FCSTD DOCUMENT  (FreeCAD 1.0R39109 (Git))
Label: L_Boxx_Old_Lid_Template
License: All rights reserved
LicenseURL: https://en.wikipedia.org/wiki/All_rights_reserved
objects: Sketcher::SketchObject×2, PartDesign::Body×1
note: 5 computed .brp shape members not serialized (recipe doc carries the construction recipe); baked Part::Feature solids carry a one-line shape summary decoded from their .brp

FEATURE [Sketcher::SketchObject] Sketch  label="SketchCutout"
  ArcFitTolerance = 0
  AttachmentSupport = -> [XY_Plane]
  FullyConstrained = true
  MakeInternals = false
  MapMode = 5
  expr: Constraints[62] = .Constraints.height
  expr: Constraints[63] = .Constraints.width / 2
  sketch-geometry (80):
    g0: LineSegment StartX=0 StartY=0 StartZ=0 EndX=0 EndY=30 EndZ=0
    g1: LineSegment StartX=0 StartY=30 StartZ=0 EndX=7 EndY=30 EndZ=0
    g2: LineSegment StartX=7 StartY=30 StartZ=0 EndX=7 EndY=49 EndZ=0
    g3: LineSegment StartX=7 StartY=49 StartZ=0 EndX=0 EndY=49 EndZ=0
    g4: LineSegment StartX=0 StartY=49 StartZ=0 EndX=0 EndY=123 EndZ=0
    g5: LineSegment StartX=0 StartY=123 StartZ=0 EndX=5 EndY=127 EndZ=0
    g6: LineSegment StartX=5 StartY=127 StartZ=0 EndX=5 EndY=147.5 EndZ=0
    g7: LineSegment StartX=5 StartY=147.5 StartZ=0 EndX=11 EndY=147.5 EndZ=0
    g8: LineSegment StartX=11 StartY=147.5 StartZ=0 EndX=11 EndY=166.5 EndZ=0
    g9: LineSegment StartX=11 StartY=166.5 StartZ=0 EndX=5 EndY=166.5 EndZ=0
    g10: LineSegment StartX=5 StartY=166.5 StartZ=0 EndX=5 EndY=187 EndZ=0
    g11: LineSegment StartX=5 StartY=187 StartZ=0 EndX=0 EndY=191 EndZ=0
    g12: LineSegment StartX=0 StartY=191 StartZ=0 EndX=0 EndY=253 EndZ=0
    g13: LineSegment StartX=0 StartY=253 StartZ=0 EndX=7 EndY=253 EndZ=0
    g14: LineSegment StartX=7 StartY=253 StartZ=0 EndX=7 EndY=272 EndZ=0
    g15: LineSegment StartX=7 StartY=272 StartZ=0 EndX=0 EndY=272 EndZ=0
    g16: LineSegment StartX=0 StartY=272 StartZ=0 EndX=0 EndY=286 EndZ=0
    g17: LineSegment StartX=0 StartY=286 StartZ=0 EndX=20.5 EndY=286 EndZ=0
    g18: LineSegment StartX=20.5 StartY=286 StartZ=0 EndX=20.5 EndY=320 EndZ=0
    g19: LineSegment [constr] StartX=5 StartY=166.5 StartZ=0 EndX=5 EndY=147.5 EndZ=0
    g20: LineSegment StartX=0 StartY=0 StartZ=0 EndX=405 EndY=0 EndZ=0
    g21: LineSegment [constr] StartX=202.5 StartY=0 StartZ=0 EndX=202.5 EndY=320 EndZ=0
    g22: LineSegment StartX=405 StartY=0 StartZ=0 EndX=405 EndY=30 EndZ=0
    g23: LineSegment StartX=405 StartY=30 StartZ=0 EndX=398 EndY=30 EndZ=0
    g24: LineSegment StartX=398 StartY=30 StartZ=0 EndX=398 EndY=49 EndZ=0
    g25: LineSegment StartX=398 StartY=49 StartZ=0 EndX=405 EndY=49 EndZ=0
    g26: LineSegment StartX=405 StartY=49 StartZ=0 EndX=405 EndY=123 EndZ=0
    g27: LineSegment StartX=405 StartY=123 StartZ=0 EndX=400 EndY=127 EndZ=0
    g28: LineSegment StartX=400 StartY=127 StartZ=0 EndX=400 EndY=147.5 EndZ=0
    g29: LineSegment StartX=400 StartY=147.5 StartZ=0 EndX=394 EndY=147.5 EndZ=0
    g30: LineSegment StartX=394 StartY=147.5 StartZ=0 EndX=394 EndY=166.5 EndZ=0
    g31: LineSegment StartX=394 StartY=166.5 StartZ=0 EndX=400 EndY=166.5 EndZ=0
    g32: LineSegment StartX=400 StartY=166.5 StartZ=0 EndX=400 EndY=187 EndZ=0
    g33: LineSegment StartX=400 StartY=187 StartZ=0 EndX=405 EndY=191 EndZ=0
    g34: LineSegment StartX=405 StartY=191 StartZ=0 EndX=405 EndY=253 EndZ=0
    g35: LineSegment StartX=405 StartY=253 StartZ=0 EndX=398 EndY=253 EndZ=0
    g36: LineSegment StartX=398 StartY=253 StartZ=0 EndX=398 EndY=272 EndZ=0
    g37: LineSegment StartX=398 StartY=272 StartZ=0 EndX=405 EndY=272 EndZ=0
    g38: LineSegment StartX=405 StartY=272 StartZ=0 EndX=405 EndY=286 EndZ=0
    g39: LineSegment StartX=405 StartY=286 StartZ=0 EndX=384.5 EndY=286 EndZ=0
    g40: LineSegment StartX=384.5 StartY=286 StartZ=0 EndX=384.5 EndY=320 EndZ=0
    g41: LineSegment [constr] StartX=400 StartY=166.5 StartZ=0 EndX=400 EndY=147.5 EndZ=0
    g42: LineSegment [constr] StartX=20.5 StartY=286 StartZ=0 EndX=384.5 EndY=286 EndZ=0
    g43: LineSegment [constr] StartX=7 StartY=272 StartZ=0 EndX=398 EndY=272 EndZ=0
    g44: LineSegment [constr] StartX=7 StartY=253 StartZ=0 EndX=398 EndY=253 EndZ=0
    g45: LineSegment [constr] StartX=0 StartY=191 StartZ=0 EndX=405 EndY=191 EndZ=0
    g46: LineSegment [constr] StartX=5 StartY=187 StartZ=0 EndX=400 EndY=187 EndZ=0
    g47: LineSegment [constr] StartX=11 StartY=166.5 StartZ=0 EndX=394 EndY=166.5 EndZ=0
    g48: LineSegment [constr] StartX=394 StartY=147.5 StartZ=0 EndX=11 EndY=147.5 EndZ=0
    g49: LineSegment [constr] StartX=7 StartY=49 StartZ=0 EndX=398 EndY=49 EndZ=0
    g50: LineSegment [constr] StartX=398 StartY=30 StartZ=0 EndX=7 EndY=30 EndZ=0
    g51: LineSegment [constr] StartX=405 StartY=123 StartZ=0 EndX=0 EndY=123 EndZ=0
    g52: LineSegment [constr] StartX=405 StartY=253 StartZ=0 EndX=405 EndY=272 EndZ=0
    g53: LineSegment StartX=20.5 StartY=320 StartZ=0 EndX=95.5 EndY=320 EndZ=0
    g54: LineSegment StartX=95.5 StartY=320 StartZ=0 EndX=95.5 EndY=318 EndZ=0
    g55: LineSegment StartX=95.5 StartY=318 StartZ=0 EndX=309.5 EndY=318 EndZ=0
    g56: LineSegment StartX=309.5 StartY=318 StartZ=0 EndX=309.5 EndY=320 EndZ=0
    g57: LineSegment StartX=309.5 StartY=320 StartZ=0 EndX=384.5 EndY=320 EndZ=0
    g58: LineSegment StartX=62 StartY=113 StartZ=0 EndX=27.5 EndY=113 EndZ=0
    g59: LineSegment StartX=27.5 StartY=113 StartZ=0 EndX=27.5 EndY=223 EndZ=0
    g60: LineSegment StartX=27.5 StartY=223 StartZ=0 EndX=62 EndY=263 EndZ=0
    g61: LineSegment StartX=62 StartY=263 StartZ=0 EndX=202.5 EndY=263 EndZ=0
    g62: LineSegment StartX=62 StartY=113 StartZ=0 EndX=62 EndY=198 EndZ=0
    g63: LineSegment StartX=62 StartY=198 StartZ=0 EndX=77.5 EndY=218 EndZ=0
    g64: LineSegment StartX=77.5 StartY=218 StartZ=0 EndX=145.5 EndY=218 EndZ=0
    g65: LineSegment StartX=145.5 StartY=218 StartZ=0 EndX=145.5 EndY=195 EndZ=0
    g66: LineSegment StartX=145.5 StartY=195 StartZ=0 EndX=202.5 EndY=195 EndZ=0
    g67: LineSegment [constr] StartX=62 StartY=263 StartZ=0 EndX=62 EndY=198 EndZ=0
    g68: LineSegment [constr] StartX=202.5 StartY=195 StartZ=0 EndX=202.5 EndY=263 EndZ=0
    g69: LineSegment StartX=343 StartY=113 StartZ=0 EndX=377.5 EndY=113 EndZ=0
    g70: LineSegment StartX=377.5 StartY=113 StartZ=0 EndX=377.5 EndY=223 EndZ=0
    g71: LineSegment StartX=377.5 StartY=223 StartZ=0 EndX=343 EndY=263 EndZ=0
    g72: LineSegment StartX=343 StartY=263 StartZ=0 EndX=202.5 EndY=263 EndZ=0
    g73: LineSegment StartX=343 StartY=113 StartZ=0 EndX=343 EndY=198 EndZ=0
    g74: LineSegment StartX=343 StartY=198 StartZ=0 EndX=327.5 EndY=218 EndZ=0
    g75: LineSegment StartX=327.5 StartY=218 StartZ=0 EndX=259.5 EndY=218 EndZ=0
    g76: LineSegment StartX=259.5 StartY=218 StartZ=0 EndX=259.5 EndY=195 EndZ=0
    g77: LineSegment StartX=259.5 StartY=195 StartZ=0 EndX=202.5 EndY=195 EndZ=0
    g78: LineSegment [constr] StartX=343 StartY=263 StartZ=0 EndX=343 EndY=198 EndZ=0
    g79: LineSegment [constr] StartX=62 StartY=198 StartZ=0 EndX=343 EndY=198 EndZ=0
  constraints (223):
    c: Coincident(g-1,g0)
    c: PointOnObject(g0,g-2)
    c: Coincident(g0,g1)
    c: Horizontal(g1)
    c: Coincident(g1,g2)
    c: Vertical(g2)
    c: Coincident(g2,g3)
    c: PointOnObject(g3,g-2)
    c: Horizontal(g3)
    c: Coincident(g3,g4)
    c: PointOnObject(g4,g-2)
    c: Coincident(g4,g5)
    c: Coincident(g5,g6)
    c: Vertical(g6)
    c: Coincident(g6,g7)
    c: Horizontal(g7)
    c: Coincident(g7,g8)
    c: Vertical(g8)
    c: Coincident(g8,g9)
    c: Horizontal(g9)
    c: Coincident(g9,g10)
    c: Vertical(g10)
    c: Coincident(g10,g11)
    c: PointOnObject(g11,g-2)
    c: Coincident(g11,g12)
    c: PointOnObject(g12,g-2)
    c: Coincident(g12,g13)
    c: Coincident(g13,g14)
    c: Vertical(g14)
    c: Coincident(g14,g15)
    c: PointOnObject(g15,g-2)
    c: Horizontal(g15)
    c: Coincident(g15,g16)
    c: Coincident(g16,g17)
    c: Horizontal(g17)
    c: Coincident(g17,g18)
    c: Vertical(g18)
    c: PointOnObject(g16,g-2)
    c: Horizontal(g13)
    c: DistanceY(g0,g18) = 320  'height'
    c: DistanceY(g18,g18) = 34
    c: DistanceY(g16,g16) = 14
    c: DistanceY(g14,g14) = 19
    c: DistanceY(g12,g12) = 62
    c: DistanceY(g4,g11) = 68
    c: Equal(g10,g6)
    c: Equal(g11,g5)
    c: Coincident(g19,g9)
    c: Coincident(g19,g6)
    c: Vertical(g19)
    c: DistanceY(g8,g8) = 19
    c: DistanceY(g5,g10) = 60
    c: DistanceX(g11,g10) = 5
    c: DistanceX(g9,g9) = 6
    c: DistanceY(g0,g0) = 30
    c: DistanceX(g1,g1) = 7
    c: Equal(g15,g3)
    c: Horizontal(g20)
    c: Coincident(g0,g20)
    c: DistanceX(g20,g20) = 405  'width'
    c: PointOnObject(g21,g20)
    c: Vertical(g21)
    c: DistanceY(g21,g21) = 320
    c: DistanceX(g0,g21) = 202.5
    c: Coincident(g22,g23)
    c: Horizontal(g23)
    c: Coincident(g23,g24)
    c: Vertical(g24)
    c: Coincident(g24,g25)
    c: Horizontal(g25)
    c: Coincident(g25,g26)
    c: Coincident(g26,g27)
    c: Coincident(g27,g28)
    c: Vertical(g28)
    c: Coincident(g28,g29)
    c: Horizontal(g29)
    c: Coincident(g29,g30)
    c: Vertical(g30)
    c: Coincident(g30,g31)
    c: Horizontal(g31)
    c: Coincident(g31,g32)
    c: Vertical(g32)
    c: Coincident(g32,g33)
    c: Coincident(g33,g34)
    c: Coincident(g34,g35)
    c: Coincident(g35,g36)
    c: Vertical(g36)
    c: Coincident(g36,g37)
    c: Horizontal(g37)
    c: Coincident(g37,g38)
    c: Coincident(g38,g39)
    c: Horizontal(g39)
    c: Coincident(g39,g40)
    c: Vertical(g40)
    c: Horizontal(g35)
    c: Equal(g32,g28)
    c: Equal(g33,g27)
    c: Coincident(g41,g31)
    c: Coincident(g41,g28)
    c: Vertical(g41)
    c: Coincident(g42,g17)
    c: Coincident(g42,g39)
    c: Horizontal(g42)
    c: Coincident(g43,g14)
    c: Coincident(g43,g36)
    c: Horizontal(g43)
    c: Coincident(g44,g13)
    c: Coincident(g44,g35)
    c: Horizontal(g44)
    c: Coincident(g45,g11)
    c: Coincident(g45,g33)
    c: Horizontal(g45)
    c: Coincident(g46,g10)
    c: Coincident(g46,g32)
    c: Horizontal(g46)
    c: Coincident(g47,g8)
    c: Coincident(g47,g30)
    c: Horizontal(g47)
    c: Coincident(g48,g29)
    c: Coincident(g48,g7)
    c: Horizontal(g48)
    c: Coincident(g22,g20)
    c: Vertical(g22)
    c: Vertical(g26)
    c: Vertical(g34)
    c: Vertical(g38)
    c: Coincident(g49,g2)
    c: Coincident(g49,g24)
    c: Horizontal(g49)
    c: Coincident(g50,g23)
    c: Coincident(g50,g1)
    c: Horizontal(g50)
    c: Equal(g1,g23)
    c: Equal(g25,g23)
    c: Coincident(g51,g26)
    c: Coincident(g51,g4)
    c: Horizontal(g51)
    c: Equal(g9,g31)
    c: DistanceX(g17,g17) = 20.5
    c: DistanceX(g32,g33) = 5
    c: Coincident(g52,g34)
    c: Coincident(g52,g37)
    c: Vertical(g52)
    c: Equal(g13,g35)
    c: Equal(g17,g39)
    c: Coincident(g18,g53)
    c: Horizontal(g53)
    c: Coincident(g53,g54)
    c: Vertical(g54)
    c: Coincident(g54,g55)
    c: Horizontal(g55)
    c: Coincident(g55,g56)
    c: Vertical(g56)
    c: Coincident(g56,g57)
    c: Coincident(g57,g40)
    c: Horizontal(g57)
    c: Equal(g53,g57)
    c: DistanceX(g53,g53) = 75
    c: DistanceY(g54,g53) = 2
    c: Horizontal(g58)
    c: Coincident(g58,g59)
    c: Vertical(g59)
    c: Coincident(g59,g60)
    c: Coincident(g60,g61)
    c: Horizontal(g61)
    c: Coincident(g58,g62)
    c: Vertical(g62)
    c: Coincident(g62,g63)
    c: Coincident(g63,g64)
    c: Horizontal(g64)
    c: Coincident(g64,g65)
    c: Vertical(g65)
    c: Coincident(g65,g66)
    c: Horizontal(g66)
    c: DistanceX(g58,g58) = 34.5
    c: DistanceY(g59,g59) = 110
    c: DistanceY(g58,g60) = 150
    c: DistanceY(g63,g60) = 45
    c: DistanceY(g62,g62) = 85
    c: DistanceY(g65,g60) = 68
    c: DistanceX(g64,g64) = 68
    c: DistanceX(g59,g64) = 118
    c: Coincident(g67,g60)
    c: Coincident(g67,g62)
    c: Vertical(g67)
    c: Coincident(g68,g66)
    c: Coincident(g68,g61)
    c: Vertical(g68)
    c: Horizontal(g69)
    c: Coincident(g69,g70)
    c: Vertical(g70)
    c: Coincident(g70,g71)
    c: Coincident(g71,g72)
    c: Horizontal(g72)
    c: Coincident(g69,g73)
    c: Vertical(g73)
    c: Coincident(g73,g74)
    c: Coincident(g74,g75)
    c: Horizontal(g75)
    c: Coincident(g75,g76)
    c: Vertical(g76)
    c: Coincident(g76,g77)
    c: Horizontal(g77)
    c: Coincident(g78,g71)
    c: Coincident(g78,g73)
    c: Vertical(g78)
    c: Equal(g66,g77)
    c: Equal(g61,g72)
    c: Equal(g65,g76)
    c: Equal(g75,g64)
    c: Equal(g62,g73)
    c: Equal(g69,g58)
    c: Equal(g70,g59)
    c: Coincident(g61,g72)
    c: Coincident(g66,g77)
    c: Coincident(g79,g62)
    c: Coincident(g79,g73)
    c: Horizontal(g79)
    c: DistanceX(g58,g69) = 350
    c: DistanceY(g0,g58) = 113
    c: DistanceX(g0,g58) = 27.5
    c: Equal(g14,g2)
    c: Equal(g40,g18)
FEATURE [Sketcher::SketchObject] Sketch001  label="SketchHoles"
  ArcFitTolerance = 0
  AttachmentSupport = -> [XY_Plane]
  FullyConstrained = true
  MakeInternals = false
  MapMode = 5
  sketch-geometry (178):
    g0: LineSegment [constr] StartX=45 StartY=25 StartZ=0 EndX=45 EndY=55.3109 EndZ=0
    g1: LineSegment [constr] StartX=45 StartY=55.3109 StartZ=0 EndX=18.75 EndY=70.4663 EndZ=0
    g2: LineSegment [constr] StartX=18.75 StartY=70.4663 StartZ=0 EndX=-7.5 EndY=55.3109 EndZ=0
    g3: LineSegment [constr] StartX=-7.5 StartY=55.3109 StartZ=0 EndX=-7.5 EndY=25 EndZ=0
    g4: LineSegment [constr] StartX=-7.5 StartY=25 StartZ=0 EndX=18.75 EndY=9.84456 EndZ=0
    g5: LineSegment [constr] StartX=18.75 StartY=9.84456 StartZ=0 EndX=45 EndY=25 EndZ=0
    g6: Circle [constr] CenterX=18.75 CenterY=40.1554 CenterZ=0 NormalX=0 NormalY=0 NormalZ=1 AngleXU=0 Radius=30.3109
    g7: LineSegment [constr] StartX=97.5 StartY=25 StartZ=0 EndX=97.5 EndY=55.3109 EndZ=0
    g8: LineSegment [constr] StartX=97.5 StartY=55.3109 StartZ=0 EndX=71.25 EndY=70.4663 EndZ=0
    g9: LineSegment [constr] StartX=71.25 StartY=70.4663 StartZ=0 EndX=45 EndY=55.3109 EndZ=0
    g10: LineSegment [constr] StartX=45 StartY=55.3109 StartZ=0 EndX=45 EndY=25 EndZ=0
    g11: LineSegment [constr] StartX=45 StartY=25 StartZ=0 EndX=71.25 EndY=9.84456 EndZ=0
    g12: LineSegment [constr] StartX=71.25 StartY=9.84456 StartZ=0 EndX=97.5 EndY=25 EndZ=0
    g13: Circle [constr] CenterX=71.25 CenterY=40.1554 CenterZ=0 NormalX=0 NormalY=0 NormalZ=1 AngleXU=0 Radius=30.3109
    g14: LineSegment [constr] StartX=150 StartY=25 StartZ=0 EndX=150 EndY=55.3109 EndZ=0
    g15: LineSegment [constr] StartX=150 StartY=55.3109 StartZ=0 EndX=123.75 EndY=70.4663 EndZ=0
    g16: LineSegment [constr] StartX=123.75 StartY=70.4663 StartZ=0 EndX=97.5 EndY=55.3109 EndZ=0
    g17: LineSegment [constr] StartX=97.5 StartY=55.3109 StartZ=0 EndX=97.5 EndY=25 EndZ=0
    g18: LineSegment [constr] StartX=97.5 StartY=25 StartZ=0 EndX=123.75 EndY=9.84456 EndZ=0
    g19: LineSegment [constr] StartX=123.75 StartY=9.84456 StartZ=0 EndX=150 EndY=25 EndZ=0
    g20: Circle [constr] CenterX=123.75 CenterY=40.1554 CenterZ=0 NormalX=0 NormalY=0 NormalZ=1 AngleXU=0 Radius=30.3109
    g21: LineSegment [constr] StartX=202.5 StartY=25 StartZ=0 EndX=202.5 EndY=55.3109 EndZ=0
    g22: LineSegment [constr] StartX=202.5 StartY=55.3109 StartZ=0 EndX=176.25 EndY=70.4663 EndZ=0
    g23: LineSegment [constr] StartX=176.25 StartY=70.4663 StartZ=0 EndX=150 EndY=55.3109 EndZ=0
    g24: LineSegment [constr] StartX=150 StartY=55.3109 StartZ=0 EndX=150 EndY=25 EndZ=0
    g25: LineSegment [constr] StartX=150 StartY=25 StartZ=0 EndX=176.25 EndY=9.84456 EndZ=0
    g26: LineSegment [constr] StartX=176.25 StartY=9.84456 StartZ=0 EndX=202.5 EndY=25 EndZ=0
    g27: Circle [constr] CenterX=176.25 CenterY=40.1554 CenterZ=0 NormalX=0 NormalY=0 NormalZ=1 AngleXU=0 Radius=30.3109
    g28: LineSegment [constr] StartX=255 StartY=25 StartZ=0 EndX=255 EndY=55.3109 EndZ=0
    g29: LineSegment [constr] StartX=255 StartY=55.3109 StartZ=0 EndX=228.75 EndY=70.4663 EndZ=0
    g30: LineSegment [constr] StartX=228.75 StartY=70.4663 StartZ=0 EndX=202.5 EndY=55.3109 EndZ=0
    g31: LineSegment [constr] StartX=202.5 StartY=55.3109 StartZ=0 EndX=202.5 EndY=25 EndZ=0
    g32: LineSegment [constr] StartX=202.5 StartY=25 StartZ=0 EndX=228.75 EndY=9.84456 EndZ=0
    g33: LineSegment [constr] StartX=228.75 StartY=9.84456 StartZ=0 EndX=255 EndY=25 EndZ=0
    g34: Circle [constr] CenterX=228.75 CenterY=40.1554 CenterZ=0 NormalX=0 NormalY=0 NormalZ=1 AngleXU=0 Radius=30.3109
    g35: LineSegment [constr] StartX=307.5 StartY=25 StartZ=0 EndX=307.5 EndY=55.3109 EndZ=0
    g36: LineSegment [constr] StartX=307.5 StartY=55.3109 StartZ=0 EndX=281.25 EndY=70.4663 EndZ=0
    g37: LineSegment [constr] StartX=281.25 StartY=70.4663 StartZ=0 EndX=255 EndY=55.3109 EndZ=0
    g38: LineSegment [constr] StartX=255 StartY=55.3109 StartZ=0 EndX=255 EndY=25 EndZ=0
    g39: LineSegment [constr] StartX=255 StartY=25 StartZ=0 EndX=281.25 EndY=9.84456 EndZ=0
    g40: LineSegment [constr] StartX=281.25 StartY=9.84456 StartZ=0 EndX=307.5 EndY=25 EndZ=0
    g41: Circle [constr] CenterX=281.25 CenterY=40.1554 CenterZ=0 NormalX=0 NormalY=0 NormalZ=1 AngleXU=0 Radius=30.3109
    g42: LineSegment [constr] StartX=360 StartY=25 StartZ=0 EndX=360 EndY=55.3109 EndZ=0
    g43: LineSegment [constr] StartX=360 StartY=55.3109 StartZ=0 EndX=333.75 EndY=70.4663 EndZ=0
    g44: LineSegment [constr] StartX=333.75 StartY=70.4663 StartZ=0 EndX=307.5 EndY=55.3109 EndZ=0
    g45: LineSegment [constr] StartX=307.5 StartY=55.3109 StartZ=0 EndX=307.5 EndY=25 EndZ=0
    g46: LineSegment [constr] StartX=307.5 StartY=25 StartZ=0 EndX=333.75 EndY=9.84456 EndZ=0
    g47: LineSegment [constr] StartX=333.75 StartY=9.84456 StartZ=0 EndX=360 EndY=25 EndZ=0
    g48: Circle [constr] CenterX=333.75 CenterY=40.1554 CenterZ=0 NormalX=0 NormalY=0 NormalZ=1 AngleXU=0 Radius=30.3109
    g49: LineSegment [constr] StartX=412.5 StartY=25 StartZ=0 EndX=412.5 EndY=55.3109 EndZ=0
    g50: LineSegment [constr] StartX=412.5 StartY=55.3109 StartZ=0 EndX=386.25 EndY=70.4663 EndZ=0
    g51: LineSegment [constr] StartX=386.25 StartY=70.4663 StartZ=0 EndX=360 EndY=55.3109 EndZ=0
    g52: LineSegment [constr] StartX=360 StartY=55.3109 StartZ=0 EndX=360 EndY=25 EndZ=0
    g53: LineSegment [constr] StartX=360 StartY=25 StartZ=0 EndX=386.25 EndY=9.84456 EndZ=0
    g54: LineSegment [constr] StartX=386.25 StartY=9.84456 StartZ=0 EndX=412.5 EndY=25 EndZ=0
    g55: Circle [constr] CenterX=386.25 CenterY=40.1554 CenterZ=0 NormalX=0 NormalY=0 NormalZ=1 AngleXU=0 Radius=30.3109
    g56: LineSegment [constr] StartX=71.25 StartY=70.4663 StartZ=0 EndX=71.25 EndY=100.777 EndZ=0
    g57: LineSegment [constr] StartX=71.25 StartY=100.777 StartZ=0 EndX=45 EndY=115.933 EndZ=0
    g58: LineSegment [constr] StartX=45 StartY=115.933 StartZ=0 EndX=18.75 EndY=100.777 EndZ=0
    g59: LineSegment [constr] StartX=18.75 StartY=100.777 StartZ=0 EndX=18.75 EndY=70.4663 EndZ=0
    g60: LineSegment [constr] StartX=18.75 StartY=70.4663 StartZ=0 EndX=45 EndY=55.3109 EndZ=0
    g61: LineSegment [constr] StartX=45 StartY=55.3109 StartZ=0 EndX=71.25 EndY=70.4663 EndZ=0
    g62: Circle [constr] CenterX=45 CenterY=85.6218 CenterZ=0 NormalX=0 NormalY=0 NormalZ=1 AngleXU=0 Radius=30.3109
    g63: LineSegment [constr] StartX=0 StartY=0 StartZ=0 EndX=18.75 EndY=9.84456 EndZ=0
    g64: LineSegment [constr] StartX=405 StartY=0 StartZ=0 EndX=386.25 EndY=9.84456 EndZ=0
    g65: LineSegment [constr] StartX=386.25 StartY=70.4663 StartZ=0 EndX=386.25 EndY=100.777 EndZ=0
    g66: LineSegment [constr] StartX=386.25 StartY=100.777 StartZ=0 EndX=360 EndY=115.933 EndZ=0
    g67: LineSegment [constr] StartX=360 StartY=115.933 StartZ=0 EndX=333.75 EndY=100.777 EndZ=0
    g68: LineSegment [constr] StartX=333.75 StartY=100.777 StartZ=0 EndX=333.75 EndY=70.4663 EndZ=0
    g69: LineSegment [constr] StartX=333.75 StartY=70.4663 StartZ=0 EndX=360 EndY=55.3109 EndZ=0
    g70: LineSegment [constr] StartX=360 StartY=55.3109 StartZ=0 EndX=386.25 EndY=70.4663 EndZ=0
    g71: Circle [constr] CenterX=360 CenterY=85.6218 CenterZ=0 NormalX=0 NormalY=0 NormalZ=1 AngleXU=0 Radius=30.3109
    g72: LineSegment [constr] StartX=228.75 StartY=70.4663 StartZ=0 EndX=228.75 EndY=100.777 EndZ=0
    g73: LineSegment [constr] StartX=228.75 StartY=100.777 StartZ=0 EndX=202.5 EndY=115.933 EndZ=0
    g74: LineSegment [constr] StartX=202.5 StartY=115.933 StartZ=0 EndX=176.25 EndY=100.777 EndZ=0
    g75: LineSegment [constr] StartX=176.25 StartY=100.777 StartZ=0 EndX=176.25 EndY=70.4663 EndZ=0
    g76: LineSegment [constr] StartX=176.25 StartY=70.4663 StartZ=0 EndX=202.5 EndY=55.3109 EndZ=0
    g77: LineSegment [constr] StartX=202.5 StartY=55.3109 StartZ=0 EndX=228.75 EndY=70.4663 EndZ=0
    g78: Circle [constr] CenterX=202.5 CenterY=85.6218 CenterZ=0 NormalX=0 NormalY=0 NormalZ=1 AngleXU=0 Radius=30.3109
    g79: Circle CenterX=45 CenterY=25 CenterZ=0 NormalX=0 NormalY=0 NormalZ=1 AngleXU=0 Radius=5
    g80: Circle CenterX=71.25 CenterY=100.777 CenterZ=0 NormalX=0 NormalY=0 NormalZ=1 AngleXU=0 Radius=5
    g81: Circle CenterX=202.5 CenterY=115.933 CenterZ=0 NormalX=0 NormalY=0 NormalZ=1 AngleXU=0 Radius=5
    g82: Circle CenterX=202.5 CenterY=25 CenterZ=0 NormalX=0 NormalY=0 NormalZ=1 AngleXU=0 Radius=3e-15
    g83: Circle CenterX=202.5 CenterY=25 CenterZ=0 NormalX=0 NormalY=0 NormalZ=1 AngleXU=0 Radius=5
    g84: Circle CenterX=333.75 CenterY=100.777 CenterZ=0 NormalX=0 NormalY=0 NormalZ=1 AngleXU=0 Radius=5
    g85: Circle CenterX=360 CenterY=25 CenterZ=0 NormalX=0 NormalY=0 NormalZ=1 AngleXU=0 Radius=5
    g86: LineSegment [constr] StartX=202.5 StartY=146.244 StartZ=0 EndX=176.25 EndY=161.399 EndZ=0
    g87: LineSegment [constr] StartX=176.25 StartY=161.399 StartZ=0 EndX=150 EndY=146.244 EndZ=0
    g88: LineSegment [constr] StartX=150 StartY=146.244 StartZ=0 EndX=150 EndY=115.933 EndZ=0
    g89: LineSegment [constr] StartX=150 StartY=115.933 StartZ=0 EndX=176.25 EndY=100.777 EndZ=0
    g90: LineSegment [constr] StartX=176.25 StartY=100.777 StartZ=0 EndX=202.5 EndY=115.933 EndZ=0
    g91: LineSegment [constr] StartX=202.5 StartY=115.933 StartZ=0 EndX=202.5 EndY=146.244 EndZ=0
    g92: Circle [constr] CenterX=176.25 CenterY=131.088 CenterZ=0 NormalX=0 NormalY=0 NormalZ=1 AngleXU=0 Radius=30.3109
    g93: LineSegment [constr] StartX=176.25 StartY=161.399 StartZ=0 EndX=176.25 EndY=191.71 EndZ=0
    g94: LineSegment [constr] StartX=176.25 StartY=191.71 StartZ=0 EndX=150 EndY=206.865 EndZ=0
    g95: LineSegment [constr] StartX=150 StartY=206.865 StartZ=0 EndX=123.75 EndY=191.71 EndZ=0
    g96: LineSegment [constr] StartX=123.75 StartY=191.71 StartZ=0 EndX=123.75 EndY=161.399 EndZ=0
    g97: LineSegment [constr] StartX=123.75 StartY=161.399 StartZ=0 EndX=150 EndY=146.244 EndZ=0
    g98: LineSegment [constr] StartX=150 StartY=146.244 StartZ=0 EndX=176.25 EndY=161.399 EndZ=0
    g99: Circle [constr] CenterX=150 CenterY=176.554 CenterZ=0 NormalX=0 NormalY=0 NormalZ=1 AngleXU=0 Radius=30.3109
    g100: Circle CenterX=123.75 CenterY=191.71 CenterZ=0 NormalX=0 NormalY=0 NormalZ=1 AngleXU=0 Radius=5
    g101: LineSegment [constr] StartX=255 StartY=115.933 StartZ=0 EndX=255 EndY=146.244 EndZ=0
    g102: LineSegment [constr] StartX=255 StartY=146.244 StartZ=0 EndX=228.75 EndY=161.399 EndZ=0
    g103: LineSegment [constr] StartX=228.75 StartY=161.399 StartZ=0 EndX=202.5 EndY=146.244 EndZ=0
    g104: LineSegment [constr] StartX=202.5 StartY=146.244 StartZ=0 EndX=202.5 EndY=115.933 EndZ=0
    g105: LineSegment [constr] StartX=202.5 StartY=115.933 StartZ=0 EndX=228.75 EndY=100.777 EndZ=0
    g106: LineSegment [constr] StartX=228.75 StartY=100.777 StartZ=0 EndX=255 EndY=115.933 EndZ=0
    g107: Circle [constr] CenterX=228.75 CenterY=131.088 CenterZ=0 NormalX=0 NormalY=0 NormalZ=1 AngleXU=0 Radius=30.3109
    g108: LineSegment [constr] StartX=281.25 StartY=161.399 StartZ=0 EndX=281.25 EndY=191.71 EndZ=0
    g109: LineSegment [constr] StartX=281.25 StartY=191.71 StartZ=0 EndX=255 EndY=206.865 EndZ=0
    g110: LineSegment [constr] StartX=255 StartY=206.865 StartZ=0 EndX=228.75 EndY=191.71 EndZ=0
    g111: LineSegment [constr] StartX=228.75 StartY=191.71 StartZ=0 EndX=228.75 EndY=161.399 EndZ=0
    g112: LineSegment [constr] StartX=228.75 StartY=161.399 StartZ=0 EndX=255 EndY=146.244 EndZ=0
    g113: LineSegment [constr] StartX=255 StartY=146.244 StartZ=0 EndX=281.25 EndY=161.399 EndZ=0
    g114: Circle [constr] CenterX=255 CenterY=176.554 CenterZ=0 NormalX=0 NormalY=0 NormalZ=1 AngleXU=0 Radius=30.3109
    g115: Circle CenterX=281.25 CenterY=191.71 CenterZ=0 NormalX=0 NormalY=0 NormalZ=1 AngleXU=0 Radius=5
    g116: LineSegment [constr] StartX=97.5 StartY=115.933 StartZ=0 EndX=97.5 EndY=146.244 EndZ=0
    g117: LineSegment [constr] StartX=97.5 StartY=146.244 StartZ=0 EndX=71.25 EndY=161.399 EndZ=0
    g118: LineSegment [constr] StartX=71.25 StartY=161.399 StartZ=0 EndX=45 EndY=146.244 EndZ=0
    g119: LineSegment [constr] StartX=45 StartY=146.244 StartZ=0 EndX=45 EndY=115.933 EndZ=0
    g120: LineSegment [constr] StartX=45 StartY=115.933 StartZ=0 EndX=71.25 EndY=100.777 EndZ=0
    g121: LineSegment [constr] StartX=71.25 StartY=100.777 StartZ=0 EndX=97.5 EndY=115.933 EndZ=0
    g122: Circle [constr] CenterX=71.25 CenterY=131.088 CenterZ=0 NormalX=0 NormalY=0 NormalZ=1 AngleXU=0 Radius=30.3109
    g123: LineSegment [constr] StartX=71.25 StartY=161.399 StartZ=0 EndX=71.25 EndY=191.71 EndZ=0
    g124: LineSegment [constr] StartX=71.25 StartY=191.71 StartZ=0 EndX=45 EndY=206.865 EndZ=0
    g125: LineSegment [constr] StartX=45 StartY=206.865 StartZ=0 EndX=18.75 EndY=191.71 EndZ=0
    g126: LineSegment [constr] StartX=18.75 StartY=191.71 StartZ=0 EndX=18.75 EndY=161.399 EndZ=0
    g127: LineSegment [constr] StartX=18.75 StartY=161.399 StartZ=0 EndX=45 EndY=146.244 EndZ=0
    g128: LineSegment [constr] StartX=45 StartY=146.244 StartZ=0 EndX=71.25 EndY=161.399 EndZ=0
    g129: Circle [constr] CenterX=45 CenterY=176.554 CenterZ=0 NormalX=0 NormalY=0 NormalZ=1 AngleXU=0 Radius=30.3109
    g130: LineSegment [constr] StartX=97.5 StartY=206.865 StartZ=0 EndX=97.5 EndY=237.176 EndZ=0
    g131: LineSegment [constr] StartX=97.5 StartY=237.176 StartZ=0 EndX=71.25 EndY=252.332 EndZ=0
    g132: LineSegment [constr] StartX=71.25 StartY=252.332 StartZ=0 EndX=45 EndY=237.176 EndZ=0
    g133: LineSegment [constr] StartX=45 StartY=237.176 StartZ=0 EndX=45 EndY=206.865 EndZ=0
    g134: LineSegment [constr] StartX=45 StartY=206.865 StartZ=0 EndX=71.25 EndY=191.71 EndZ=0
    g135: LineSegment [constr] StartX=71.25 StartY=191.71 StartZ=0 EndX=97.5 EndY=206.865 EndZ=0
    g136: Circle [constr] CenterX=71.25 CenterY=222.021 CenterZ=0 NormalX=0 NormalY=0 NormalZ=1 AngleXU=0 Radius=30.3109
    g137: LineSegment [constr] StartX=71.25 StartY=252.332 StartZ=0 EndX=71.25 EndY=282.643 EndZ=0
    g138: LineSegment [constr] StartX=71.25 StartY=282.643 StartZ=0 EndX=45 EndY=297.798 EndZ=0
    g139: LineSegment [constr] StartX=45 StartY=297.798 StartZ=0 EndX=18.75 EndY=282.643 EndZ=0
    g140: LineSegment [constr] StartX=18.75 StartY=282.643 StartZ=0 EndX=18.75 EndY=252.332 EndZ=0
    g141: LineSegment [constr] StartX=18.75 StartY=252.332 StartZ=0 EndX=45 EndY=237.176 EndZ=0
    g142: LineSegment [constr] StartX=45 StartY=237.176 StartZ=0 EndX=71.25 EndY=252.332 EndZ=0
    g143: Circle [constr] CenterX=45 CenterY=267.487 CenterZ=0 NormalX=0 NormalY=0 NormalZ=1 AngleXU=0 Radius=30.3109
    g144: Circle CenterX=45 CenterY=297.798 CenterZ=0 NormalX=0 NormalY=0 NormalZ=1 AngleXU=0 Radius=5
    g145: LineSegment [constr] StartX=360 StartY=115.933 StartZ=0 EndX=360 EndY=146.244 EndZ=0
    g146: LineSegment [constr] StartX=360 StartY=146.244 StartZ=0 EndX=333.75 EndY=161.399 EndZ=0
    g147: LineSegment [constr] StartX=333.75 StartY=161.399 StartZ=0 EndX=307.5 EndY=146.244 EndZ=0
    g148: LineSegment [constr] StartX=307.5 StartY=146.244 StartZ=0 EndX=307.5 EndY=115.933 EndZ=0
    g149: LineSegment [constr] StartX=307.5 StartY=115.933 StartZ=0 EndX=333.75 EndY=100.777 EndZ=0
    g150: LineSegment [constr] StartX=333.75 StartY=100.777 StartZ=0 EndX=360 EndY=115.933 EndZ=0
    g151: Circle [constr] CenterX=333.75 CenterY=131.088 CenterZ=0 NormalX=0 NormalY=0 NormalZ=1 AngleXU=0 Radius=30.3109
    g152: LineSegment [constr] StartX=360 StartY=146.244 StartZ=0 EndX=386.25 EndY=161.399 EndZ=0
    g153: LineSegment [constr] StartX=386.25 StartY=161.399 StartZ=0 EndX=386.25 EndY=191.71 EndZ=0
    g154: LineSegment [constr] StartX=386.25 StartY=191.71 StartZ=0 EndX=360 EndY=206.865 EndZ=0
    g155: LineSegment [constr] StartX=360 StartY=206.865 StartZ=0 EndX=333.75 EndY=191.71 EndZ=0
    g156: LineSegment [constr] StartX=333.75 StartY=191.71 StartZ=0 EndX=333.75 EndY=161.399 EndZ=0
    g157: LineSegment [constr] StartX=333.75 StartY=161.399 StartZ=0 EndX=360 EndY=146.244 EndZ=0
    g158: Circle [constr] CenterX=360 CenterY=176.554 CenterZ=0 NormalX=0 NormalY=0 NormalZ=1 AngleXU=0 Radius=30.3109
    g159: LineSegment [constr] StartX=360 StartY=206.865 StartZ=0 EndX=360 EndY=237.176 EndZ=0
    g160: LineSegment [constr] StartX=360 StartY=237.176 StartZ=0 EndX=333.75 EndY=252.332 EndZ=0
    g161: LineSegment [constr] StartX=333.75 StartY=252.332 StartZ=0 EndX=307.5 EndY=237.176 EndZ=0
    g162: LineSegment [constr] StartX=307.5 StartY=237.176 StartZ=0 EndX=307.5 EndY=206.865 EndZ=0
    g163: LineSegment [constr] StartX=307.5 StartY=206.865 StartZ=0 EndX=333.75 EndY=191.71 EndZ=0
    g164: LineSegment [constr] StartX=333.75 StartY=191.71 StartZ=0 EndX=360 EndY=206.865 EndZ=0
    g165: Circle [constr] CenterX=333.75 CenterY=222.021 CenterZ=0 NormalX=0 NormalY=0 NormalZ=1 AngleXU=0 Radius=30.3109
    g166: LineSegment [constr] StartX=333.75 StartY=252.332 StartZ=0 EndX=360 EndY=237.176 EndZ=0
    g167: LineSegment [constr] StartX=360 StartY=237.176 StartZ=0 EndX=386.25 EndY=252.332 EndZ=0
    g168: LineSegment [constr] StartX=386.25 StartY=252.332 StartZ=0 EndX=386.25 EndY=282.643 EndZ=0
    g169: LineSegment [constr] StartX=386.25 StartY=282.643 StartZ=0 EndX=360 EndY=297.798 EndZ=0
    g170: LineSegment [constr] StartX=360 StartY=297.798 StartZ=0 EndX=333.75 EndY=282.643 EndZ=0
    g171: LineSegment [constr] StartX=333.75 StartY=282.643 StartZ=0 EndX=333.75 EndY=252.332 EndZ=0
    g172: Circle [constr] CenterX=360 CenterY=267.487 CenterZ=0 NormalX=0 NormalY=0 NormalZ=1 AngleXU=0 Radius=30.3109
    g173: Circle CenterX=360 CenterY=297.798 CenterZ=0 NormalX=0 NormalY=0 NormalZ=1 AngleXU=0 Radius=5
    g174: LineSegment [constr] StartX=45 StartY=297.798 StartZ=0 EndX=202.5 EndY=297.798 EndZ=0
    g175: LineSegment [constr] StartX=360 StartY=297.798 StartZ=0 EndX=202.5 EndY=297.798 EndZ=0
    g176: LineSegment [constr] StartX=202.5 StartY=297.798 StartZ=0 EndX=202.5 EndY=115.933 EndZ=0
    g177: Circle CenterX=202.5 CenterY=297.798 CenterZ=0 NormalX=0 NormalY=0 NormalZ=1 AngleXU=0 Radius=5
  constraints (394):
    c: Coincident(g0,g1)
    c: Coincident(g1,g2)
    c: Coincident(g2,g3)
    c: Coincident(g3,g4)
    c: Coincident(g4,g5)
    c: Coincident(g5,g0)
    c: Equal(g0, g1-g5) x5
    c: PointOnObject(g0,g6)
    c: PointOnObject(g1,g6)
    c: PointOnObject(g2,g6)
    c: PointOnObject(g3,g6)
    c: PointOnObject(g4,g6)
    c: PointOnObject(g5,g6)
    c: Vertical(g3)
    c: Coincident(g7,g8)
    c: Coincident(g8,g9)
    c: Coincident(g9,g10)
    c: Coincident(g10,g11)
    c: Coincident(g11,g12)
    c: Coincident(g12,g7)
    c: Equal(g7, g8-g12) x5
    c: PointOnObject(g7,g13)
    c: PointOnObject(g8,g13)
    c: PointOnObject(g9,g13)
    c: PointOnObject(g10,g13)
    c: PointOnObject(g11,g13)
    c: PointOnObject(g12,g13)
    c: Vertical(g10)
    c: Coincident(g14,g15)
    c: Coincident(g15,g16)
    c: Coincident(g16,g17)
    c: Coincident(g17,g18)
    c: Coincident(g18,g19)
    c: Coincident(g19,g14)
    c: Equal(g14, g15-g19) x5
    c: PointOnObject(g14,g20)
    c: PointOnObject(g15,g20)
    c: PointOnObject(g16,g20)
    c: PointOnObject(g17,g20)
    c: PointOnObject(g18,g20)
    c: PointOnObject(g19,g20)
    c: Vertical(g17)
    c: Coincident(g21,g22)
    c: Coincident(g22,g23)
    c: Coincident(g23,g24)
    c: Coincident(g24,g25)
    c: Coincident(g25,g26)
    c: Coincident(g26,g21)
    c: Equal(g21, g22-g26) x5
    c: PointOnObject(g21,g27)
    c: PointOnObject(g22,g27)
    c: PointOnObject(g23,g27)
    c: PointOnObject(g24,g27)
    c: PointOnObject(g25,g27)
    c: PointOnObject(g26,g27)
    c: Vertical(g24)
    c: Coincident(g28,g29)
    c: Coincident(g29,g30)
    c: Coincident(g30,g31)
    c: Coincident(g31,g32)
    c: Coincident(g32,g33)
    c: Coincident(g33,g28)
    c: Equal(g28, g29-g33) x5
    c: PointOnObject(g28,g34)
    c: PointOnObject(g29,g34)
    c: PointOnObject(g30,g34)
    c: PointOnObject(g31,g34)
    c: PointOnObject(g32,g34)
    c: PointOnObject(g33,g34)
    c: Vertical(g31)
    c: Coincident(g35,g36)
    c: Coincident(g36,g37)
    c: Coincident(g37,g38)
    c: Coincident(g38,g39)
    c: Coincident(g39,g40)
    c: Coincident(g40,g35)
    c: Equal(g35, g36-g40) x5
    c: PointOnObject(g35,g41)
    c: PointOnObject(g36,g41)
    c: PointOnObject(g37,g41)
    c: PointOnObject(g38,g41)
    c: PointOnObject(g39,g41)
    c: PointOnObject(g40,g41)
    c: Vertical(g38)
    c: Coincident(g42,g43)
    c: Coincident(g43,g44)
    c: Coincident(g44,g45)
    c: Coincident(g45,g46)
    c: Coincident(g46,g47)
    c: Coincident(g47,g42)
    c: Equal(g42, g43-g47) x5
    c: PointOnObject(g42,g48)
    c: PointOnObject(g43,g48)
    c: PointOnObject(g44,g48)
    c: PointOnObject(g45,g48)
    c: PointOnObject(g46,g48)
    c: PointOnObject(g47,g48)
    c: Vertical(g45)
    c: Coincident(g49,g50)
    c: Coincident(g50,g51)
    c: Coincident(g51,g52)
    c: Coincident(g52,g53)
    c: Coincident(g53,g54)
    c: Coincident(g54,g49)
    c: Equal(g49, g50-g54) x5
    c: PointOnObject(g49,g55)
    c: PointOnObject(g50,g55)
    c: PointOnObject(g51,g55)
    c: PointOnObject(g52,g55)
    c: PointOnObject(g53,g55)
    c: PointOnObject(g54,g55)
    c: Vertical(g52)
    c: Coincident(g9,g0)
    c: Equal(g4,g11)
    c: Equal(g4,g18)
    c: Equal(g4,g25)
    c: Equal(g4,g32)
    c: Equal(g4,g39)
    c: Equal(g4,g46)
    c: Equal(g4,g53)
    c: Coincident(g51,g42)
    c: Coincident(g16,g7)
    c: Coincident(g23,g14)
    c: Coincident(g35,g44)
    c: Coincident(g37,g28)
    c: Coincident(g30,g21)
    c: Coincident(g56,g57)
    c: Coincident(g57,g58)
    c: Coincident(g58,g59)
    c: Coincident(g59,g60)
    c: Coincident(g60,g61)
    c: Coincident(g61,g56)
    c: Equal(g56, g57-g61) x5
    c: PointOnObject(g56,g62)
    c: PointOnObject(g57,g62)
    c: PointOnObject(g58,g62)
    c: PointOnObject(g59,g62)
    c: PointOnObject(g60,g62)
    c: PointOnObject(g61,g62)
    c: Vertical(g59)
    c: Equal(g4,g60)
    c: Coincident(g59,g1)
    c: Distance(g4,g56) = 105
    c: Coincident(g63,g-1)
    c: Coincident(g63,g4)
    c: Coincident(g64,g53)
    c: Equal(g63,g64)
    c: DistanceY(g63,g0) = 25
    c: Coincident(g65,g66)
    c: Coincident(g66,g67)
    c: Coincident(g67,g68)
    c: Coincident(g68,g69)
    c: Coincident(g69,g70)
    c: Coincident(g70,g65)
    c: Equal(g65, g66-g70) x5
    c: PointOnObject(g65,g71)
    c: PointOnObject(g66,g71)
    c: PointOnObject(g67,g71)
    c: PointOnObject(g68,g71)
    c: PointOnObject(g69,g71)
    c: PointOnObject(g70,g71)
    c: Coincident(g72,g73)
    c: Coincident(g73,g74)
    c: Coincident(g74,g75)
    c: Coincident(g75,g76)
    c: Coincident(g76,g77)
    c: Coincident(g77,g72)
    c: Equal(g72, g73-g77) x5
    c: PointOnObject(g72,g78)
    c: PointOnObject(g73,g78)
    c: PointOnObject(g74,g78)
    c: PointOnObject(g75,g78)
    c: PointOnObject(g76,g78)
    c: PointOnObject(g77,g78)
    c: Equal(g76,g11)
    c: Equal(g69,g11)
    c: Vertical(g75)
    c: Vertical(g68)
    c: Coincident(g22,g75)
    c: Coincident(g65,g50)
    c: Coincident(g79,g0)
    c: Coincident(g80,g56)
    c: Coincident(g81,g73)
    c: Coincident(g82,g21)
    c: Tangent(g82,g34)
    c: Coincident(g83,g82)
    c: Coincident(g84,g67)
    c: Coincident(g85,g42)
    c: Equal(g80,g79)
    c: Equal(g80,g81)
    c: Equal(g81,g83)
    c: Equal(g81,g84)
    c: Equal(g84,g85)
    c: Diameter(g79) = 10
    c: DistanceY(g59,g59) = 30.3109  'side'
    c: Coincident(g86,g87)
    c: Coincident(g87,g88)
    c: Coincident(g88,g89)
    c: Coincident(g89,g90)
    c: Coincident(g90,g91)
    c: Coincident(g91,g86)
    c: Equal(g86, g87-g91) x5
    c: PointOnObject(g86,g92)
    c: PointOnObject(g87,g92)
    c: PointOnObject(g88,g92)
    c: PointOnObject(g89,g92)
    c: PointOnObject(g90,g92)
    c: PointOnObject(g91,g92)
    c: Coincident(g90,g81)
    c: Coincident(g89,g74)
    c: Coincident(g93,g94)
    c: Coincident(g94,g95)
    c: Coincident(g95,g96)
    c: Coincident(g96,g97)
    c: Coincident(g97,g98)
    c: Coincident(g98,g93)
    c: Equal(g93, g94-g98) x5
    c: PointOnObject(g93,g99)
    c: PointOnObject(g94,g99)
    c: PointOnObject(g95,g99)
    c: PointOnObject(g96,g99)
    c: PointOnObject(g97,g99)
    c: PointOnObject(g98,g99)
    c: Coincident(g97,g87)
    c: Coincident(g86,g93)
    c: Coincident(g100,g95)
    c: Equal(g80,g100)
    c: Coincident(g101,g102)
    c: Coincident(g102,g103)
    c: Coincident(g103,g104)
    c: Coincident(g104,g105)
    c: Coincident(g105,g106)
    c: Coincident(g106,g101)
    c: Equal(g101, g102-g106) x5
    c: PointOnObject(g101,g107)
    c: PointOnObject(g102,g107)
    c: PointOnObject(g103,g107)
    c: PointOnObject(g104,g107)
    c: PointOnObject(g105,g107)
    c: PointOnObject(g106,g107)
    c: Coincident(g86,g103)
    c: Coincident(g104,g81)
    c: Coincident(g108,g109)
    c: Coincident(g109,g110)
    c: Coincident(g110,g111)
    c: Coincident(g111,g112)
    c: Coincident(g112,g113)
    c: Coincident(g113,g108)
    c: Equal(g108, g109-g113) x5
    c: PointOnObject(g108,g114)
    c: PointOnObject(g109,g114)
    c: PointOnObject(g110,g114)
    c: PointOnObject(g111,g114)
    c: PointOnObject(g112,g114)
    c: PointOnObject(g113,g114)
    c: Coincident(g112,g101)
    c: Coincident(g102,g111)
    c: Coincident(g115,g108)
    c: Equal(g115,g100)
    c: Coincident(g116,g117)
    c: Coincident(g117,g118)
    c: Coincident(g118,g119)
    c: Coincident(g119,g120)
    c: Coincident(g120,g121)
    c: Coincident(g121,g116)
    c: Equal(g116, g117-g121) x5
    c: PointOnObject(g116,g122)
    c: PointOnObject(g117,g122)
    c: PointOnObject(g118,g122)
    c: PointOnObject(g119,g122)
    c: PointOnObject(g120,g122)
    c: PointOnObject(g121,g122)
    c: Coincident(g120,g80)
    c: Coincident(g119,g57)
    c: Coincident(g123,g124)
    c: Coincident(g124,g125)
    c: Coincident(g125,g126)
    c: Coincident(g126,g127)
    c: Coincident(g127,g128)
    c: Coincident(g128,g123)
    c: Equal(g123, g124-g128) x5
    c: PointOnObject(g123,g129)
    c: PointOnObject(g124,g129)
    c: PointOnObject(g125,g129)
    c: PointOnObject(g126,g129)
    c: PointOnObject(g127,g129)
    c: PointOnObject(g128,g129)
    c: Coincident(g127,g118)
    c: Coincident(g123,g117)
    c: Coincident(g130,g131)
    c: Coincident(g131,g132)
    c: Coincident(g132,g133)
    c: Coincident(g133,g134)
    c: Coincident(g134,g135)
    c: Coincident(g135,g130)
    c: Equal(g130, g131-g135) x5
    c: PointOnObject(g130,g136)
    c: PointOnObject(g131,g136)
    c: PointOnObject(g132,g136)
    c: PointOnObject(g133,g136)
    c: PointOnObject(g134,g136)
    c: PointOnObject(g135,g136)
    c: Coincident(g134,g123)
    c: Coincident(g133,g124)
    c: Coincident(g137,g138)
    c: Coincident(g138,g139)
    c: Coincident(g139,g140)
    c: Coincident(g140,g141)
    c: Coincident(g141,g142)
    c: Coincident(g142,g137)
    c: Equal(g137, g138-g142) x5
    c: PointOnObject(g137,g143)
    c: PointOnObject(g138,g143)
    c: PointOnObject(g139,g143)
    c: PointOnObject(g140,g143)
    c: PointOnObject(g141,g143)
    c: PointOnObject(g142,g143)
    c: Coincident(g141,g132)
    c: Coincident(g131,g137)
    c: Coincident(g144,g138)
    c: Equal(g144,g100)
    c: Coincident(g145,g146)
    c: Coincident(g146,g147)
    c: Coincident(g147,g148)
    c: Coincident(g148,g149)
    c: Coincident(g149,g150)
    c: Coincident(g150,g145)
    c: Equal(g145, g146-g150) x5
    c: PointOnObject(g145,g151)
    c: PointOnObject(g146,g151)
    c: PointOnObject(g147,g151)
    c: PointOnObject(g148,g151)
    c: PointOnObject(g149,g151)
    c: PointOnObject(g150,g151)
    c: Coincident(g145,g66)
    c: Coincident(g84,g149)
    c: Coincident(g152,g153)
    c: Coincident(g153,g154)
    c: Coincident(g154,g155)
    c: Coincident(g155,g156)
    c: Coincident(g156,g157)
    c: Coincident(g157,g152)
    c: Equal(g152, g153-g157) x5
    c: PointOnObject(g152,g158)
    c: PointOnObject(g153,g158)
    c: PointOnObject(g154,g158)
    c: PointOnObject(g155,g158)
    c: PointOnObject(g156,g158)
    c: PointOnObject(g157,g158)
    c: Coincident(g152,g145)
    c: Coincident(g156,g146)
    c: Coincident(g159,g160)
    c: Coincident(g160,g161)
    c: Coincident(g161,g162)
    c: Coincident(g162,g163)
    c: Coincident(g163,g164)
    c: Coincident(g164,g159)
    c: Equal(g159, g160-g164) x5
    c: PointOnObject(g159,g165)
    c: PointOnObject(g160,g165)
    c: PointOnObject(g161,g165)
    c: PointOnObject(g162,g165)
    c: PointOnObject(g163,g165)
    c: PointOnObject(g164,g165)
    c: Coincident(g159,g154)
    c: Coincident(g163,g155)
    c: Coincident(g166,g167)
    c: Coincident(g167,g168)
    c: Coincident(g168,g169)
    c: Coincident(g169,g170)
    c: Coincident(g170,g171)
    c: Coincident(g171,g166)
    c: Equal(g166, g167-g171) x5
    c: PointOnObject(g166,g172)
    c: PointOnObject(g167,g172)
    c: PointOnObject(g168,g172)
    c: PointOnObject(g169,g172)
    c: PointOnObject(g170,g172)
    c: PointOnObject(g171,g172)
    c: Coincident(g166,g159)
    c: Coincident(g166,g160)
    c: Coincident(g173,g169)
    c: Equal(g144,g173)
    c: Coincident(g174,g144)
    c: Horizontal(g174)
    c: Coincident(g175,g173)
    c: Coincident(g175,g174)
    c: Coincident(g176,g174)
    c: Coincident(g176,g81)
    c: Vertical(g176)
    c: Coincident(g177,g174)
    c: Equal(g177,g144)
    c: DistanceX(g63,g64) = 405
    c: PointOnObject(g64,g-1)
FEATURE [PartDesign::Body] Body
  AllowCompound = false
  Group = -> [Sketch,Sketch001]
  Origin = -> Origin
